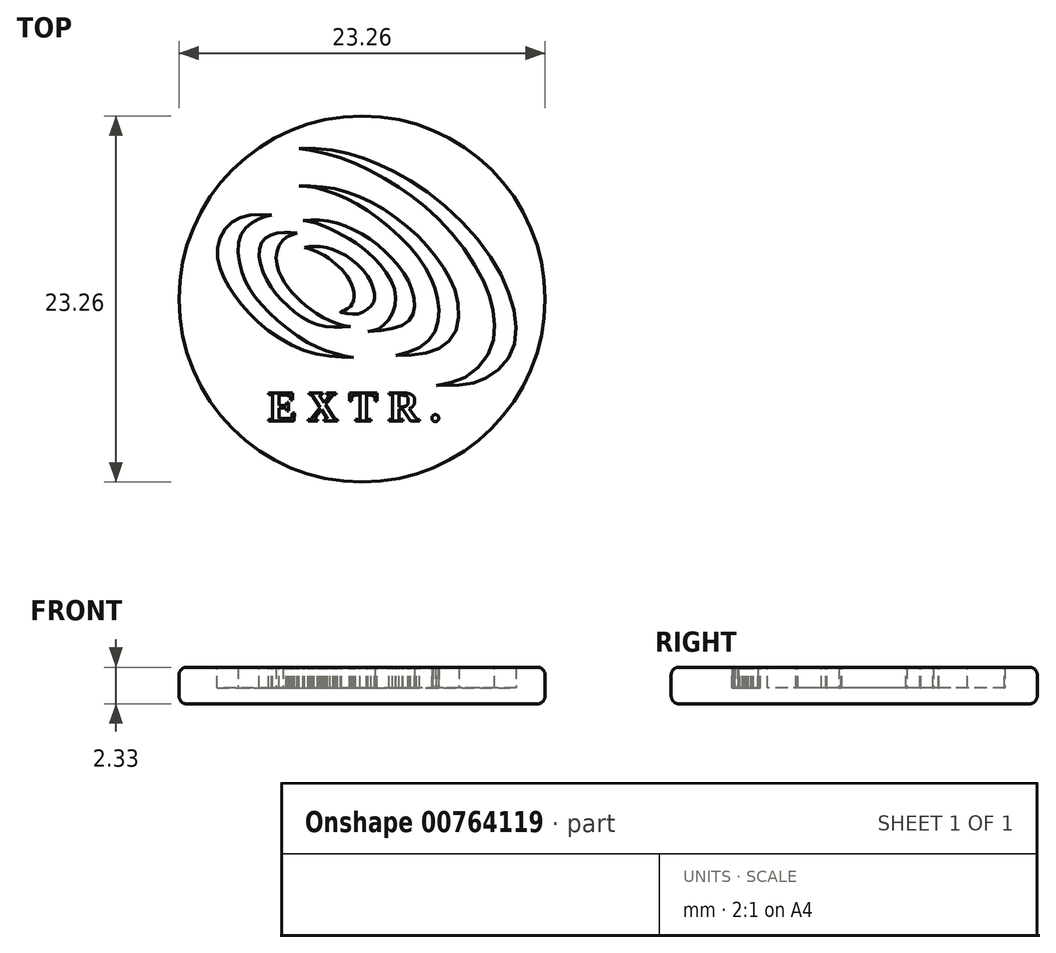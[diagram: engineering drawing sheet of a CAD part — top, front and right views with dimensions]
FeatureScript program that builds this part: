
annotation { "Feature Type Name" : "Feature", "Feature Type Description" : "" }
export const myFeature = defineFeature(function(context is Context, id is Id, definition is map)
    precondition{}
    {
        {
            assignVariable(context, id + "F0", {"name" : "Spessore", "anyValue" : 2.33});
        }
        {
            var Q0;
            Q0=qCreatedBy(makeId("Top.planeOp"),FACE);
            var sketch = newSketch(context, id + "F1", { "sketchPlane" : qUnion([Q0])});
            skCircle(sketch, "E0", {"center": v(0, 0) * mm, "radius": 11.62 * mm});
            skSolve(sketch);
        }
        {
            var Q0;
            Q0=makeQuery(id+"F1.imprint","IMPRINT",FACE,{"disambiguationData":[TD([[makeQuery(id+"F1.imprint","IMPRINT",EDGE,{"derivedFrom":sQuery(id+"F1.wireOp",EDGE,"E0")}),1.0]])]});
            extrude(context, id + "F2", {"entities" : qUnion([Q0]), "depth" : (getVariable(context, 'Spessore')) * mm, "offsetDistance" : 25 * mm});
        }
        {
            var Q0;
            Q0=makeQuery(id+"F2.opExtrude","CAP_EDGE",EDGE,{"disambiguationData":[OSD([sQuery(id+"F1.wireOp",EDGE,"E0")])],"isStart":true});
            var Q1;
            Q1=makeQuery(id+"F2.opExtrude","CAP_EDGE",EDGE,{"disambiguationData":[OSD([sQuery(id+"F1.wireOp",EDGE,"E0")])],"isStart":false});
            fillet(context, id + "F3", {"entities" : qUnion([Q0, Q1]), "radius" : .5 * mm, "tangentPropagation" : true, "allowEdgeOverflow" : false});
        }
        {
            var Q0;
            Q0=makeQuery(id+"F2.opExtrude","CAP_FACE",FACE,{"disambiguationData":[OSD([sQuery(id+"F1.wireOp",EDGE,"E0")])],"isStart":false});
            var sketch = newSketch(context, id + "F4", { "sketchPlane" : qUnion([Q0])});
            skFitSpline(sketch, "E1", {"points": [v(-4.15, 9.54) * mm, v(-1.9, 9.48) * mm, v(0.33, 8.86) * mm, v(2.32, 7.94) * mm, v(5.34, 5.86) * mm, v(8.2, 2.63) * mm, v(9.52, -0.22) * mm, v(9.72, -2.68) * mm, v(8.82, -4.33) * mm, v(7.32, -5.25) * mm, v(4.51, -5.5) * mm], "startDerivative": vector(24.3, 2.05) * mm, "endDerivative": vector(-46.96, -0.52) * mm});
            skFitSpline(sketch, "E2", {"points": [v(-4.17, 9.57) * mm, v(-2.58, 9.32) * mm, v(-0.42, 8.61) * mm, v(1.78, 7.45) * mm, v(3.82, 6.03) * mm, v(6.13, 3.65) * mm, v(7.85, 0.83) * mm, v(8.4, -1.19) * mm, v(8.13, -3.28) * mm, v(6.47, -5) * mm, v(4.52, -5.54) * mm], "startDerivative": vector(18.62, -2.24) * mm, "endDerivative": vector(-21.4, -4.3) * mm});
            skFitSpline(sketch, "E3", {"points": [v(-4.01, 7.2) * mm, v(-2.3, 7.1) * mm, v(-0.42, 6.62) * mm, v(1.63, 5.53) * mm, v(3.67, 3.88) * mm, v(5.06, 2.18) * mm, v(5.94, 0.42) * mm, v(6, -1.87) * mm, v(4.74, -3.21) * mm, v(2.17, -3.59) * mm], "startDerivative": vector(17.18, -0.33) * mm, "endDerivative": vector(-22.8, -0.77) * mm});
            skFitSpline(sketch, "E4", {"points": [v(-4.01, 7.2) * mm, v(-2.88, 7.06) * mm, v(-1.05, 6.4) * mm, v(1.04, 5.13) * mm, v(3.35, 2.94) * mm, v(4.53, 0.94) * mm, v(4.88, -0.87) * mm, v(4.23, -2.65) * mm, v(2.17, -3.59) * mm], "startDerivative": vector(11.55, -0.7) * mm, "endDerivative": vector(-17.99, -4.52) * mm});
            skFitSpline(sketch, "E5", {"points": [v(-3.73, 4.99) * mm, v(-2.39, 5) * mm, v(-0.8, 4.52) * mm, v(0.7, 3.68) * mm, v(2.18, 2.28) * mm, v(3.03, 0.97) * mm, v(3.33, -0.5) * mm, v(2.81, -1.53) * mm, v(0.37, -2.07) * mm], "startDerivative": vector(11.68, 1.03) * mm, "endDerivative": vector(-18.56, -1.71) * mm});
            skFitSpline(sketch, "E6", {"points": [v(-3.73, 4.99) * mm, v(-2.7, 4.75) * mm, v(-1.4, 4.16) * mm, v(-0.26, 3.46) * mm, v(0.97, 2.4) * mm, v(2.06, 0.62) * mm, v(1.9, -0.97) * mm, v(1.08, -1.86) * mm, v(0.37, -2.07) * mm], "startDerivative": vector(9.12, -1.58) * mm, "endDerivative": vector(-7.65, -1.26) * mm});
            skFitSpline(sketch, "E7", {"points": [v(-3.65, 3.29) * mm, v(-2.63, 3.33) * mm, v(-1.08, 2.78) * mm, v(0.35, 1.46) * mm, v(0.81, 0.15) * mm, v(0.59, -0.41) * mm, v(-0.18, -0.92) * mm, v(-1.31, -0.85) * mm], "startDerivative": vector(7.37, 1.02) * mm, "endDerivative": vector(-8.47, 1.72) * mm});
            skFitSpline(sketch, "E8", {"points": [v(-3.65, 3.29) * mm, v(-2.6, 2.89) * mm, v(-1.6, 2.16) * mm, v(-0.89, 1.36) * mm, v(-0.5, 0.22) * mm, v(-0.72, -0.45) * mm, v(-1.29, -0.79) * mm], "startDerivative": vector(5.9, -1.77) * mm, "endDerivative": vector(-4.6, -2.02) * mm});
            skFitSpline(sketch, "E9", {"points": [v(-1.29, -0.79) * mm, v(-1.31, -0.85) * mm], "startDerivative": vector(-0.1, -0.03) * mm, "endDerivative": vector(0.33, -0.05) * mm});
            skFitSpline(sketch, "E10", {"points": [v(-4.12, 4.18) * mm, v(-4.95, 3.82) * mm, v(-5.43, 2.87) * mm, v(-5.22, 1.61) * mm, v(-4.6, 0.6) * mm, v(-3.8, -0.21) * mm, v(-2.65, -1.07) * mm, v(-1.38, -1.62) * mm, v(-0.73, -1.74) * mm], "startDerivative": vector(-7.94, -2.2) * mm, "endDerivative": vector(6.18, -0.74) * mm});
            skFitSpline(sketch, "E11", {"points": [v(-4.12, 4.18) * mm, v(-5.32, 4.2) * mm, v(-6.28, 3.73) * mm, v(-6.51, 2.47) * mm, v(-5.75, 0.74) * mm, v(-4.42, -0.7) * mm, v(-2.62, -1.68) * mm, v(-0.73, -1.74) * mm], "startDerivative": vector(-9.7, 0.88) * mm, "endDerivative": vector(12.13, 0.46) * mm});
            skFitSpline(sketch, "E12", {"points": [v(-5.74, 5.35) * mm, v(-7.53, 5.26) * mm, v(-8.76, 4.35) * mm, v(-9.19, 2.78) * mm, v(-8.64, 1.11) * mm, v(-7.58, -0.42) * mm, v(-5.71, -2.17) * mm, v(-3, -3.46) * mm, v(-0.55, -3.7) * mm], "startDerivative": vector(-15.98, 0.97) * mm, "endDerivative": vector(17.67, -0.33) * mm});
            skFitSpline(sketch, "E13", {"points": [v(-5.74, 5.35) * mm, v(-6.53, 5.1) * mm, v(-7.38, 4.51) * mm, v(-7.86, 3.45) * mm, v(-7.63, 1.69) * mm, v(-6.97, 0.38) * mm, v(-5.74, -1.03) * mm, v(-3.67, -2.63) * mm, v(-1.94, -3.4) * mm, v(-0.55, -3.7) * mm], "startDerivative": vector(-9.77, -1.74) * mm, "endDerivative": vector(12.64, -2.27) * mm});
            skSolve(sketch);
        }
        {
            var Q0;
            Q0=makeQuery(id+"F4.imprint","IMPRINT",FACE,{"disambiguationData":[TD([[makeQuery(id+"F4.imprint","IMPRINT",EDGE,{"derivedFrom":sQuery(id+"F4.wireOp",EDGE,"E7")}),-1.0]])]});
            var Q1;
            Q1=makeQuery(id+"F4.imprint","IMPRINT",FACE,{"disambiguationData":[TD([[makeQuery(id+"F4.imprint","IMPRINT",EDGE,{"derivedFrom":sQuery(id+"F4.wireOp",EDGE,"E10")}),-1.0]])]});
            var Q2;
            Q2=makeQuery(id+"F4.imprint","IMPRINT",FACE,{"disambiguationData":[TD([[makeQuery(id+"F4.imprint","IMPRINT",EDGE,{"derivedFrom":sQuery(id+"F4.wireOp",EDGE,"E12")}),1.0]])]});
            var Q3;
            Q3=makeQuery(id+"F4.imprint","IMPRINT",FACE,{"disambiguationData":[TD([[makeQuery(id+"F4.imprint","IMPRINT",EDGE,{"derivedFrom":sQuery(id+"F4.wireOp",EDGE,"E5")}),-1.0]])]});
            var Q4;
            Q4=makeQuery(id+"F4.imprint","IMPRINT",FACE,{"disambiguationData":[TD([[makeQuery(id+"F4.imprint","IMPRINT",EDGE,{"derivedFrom":sQuery(id+"F4.wireOp",EDGE,"E3")}),-1.0]])]});
            var Q5;
            {var subQ0=sQuery(id+"F4.wireOp",EDGE,"E2");var subQ1=sQuery(id+"F4.wireOp",EDGE,"E1");var subQ2=makeQuery(id+"F4.imprint","INTERSECT",VERTEX,{"disambiguationData":[OD(0.0)],"derivedFrom":[subQ1,subQ0]});Q5=makeQuery(id+"F4.imprint","IMPRINT",FACE,{"disambiguationData":[TD([[makeQuery(id+"F4.imprint","IMPRINT",EDGE,{"disambiguationData":[TD([[subQ2,-1.0]])],"derivedFrom":subQ1}),-1.0]])]});}
            extrude(context, id + "F5", {"entities" : qUnion([Q0, Q1, Q2, Q3, Q4, Q5]), "operationType" : NewBodyOperationType.REMOVE, "oppositeDirection" : true, "depth" : 1.3 * mm, "offsetDistance" : 25 * mm});
        }
        {
            var Q0;
            Q0=makeQuery(id+"F2.opExtrude","CAP_FACE",FACE,{"disambiguationData":[OSD([sQuery(id+"F1.wireOp",EDGE,"E0")])],"isStart":false});
            var sketch = newSketch(context, id + "F6", { "sketchPlane" : qUnion([Q0])});
            skText(sketch, "E14", { "text": "E X T R .", "fontName": "Tinos-Bold.ttf"});
            const initialGuessF6  = {"E14": [-0.00597, -0.00774, 1, 0, 0.00196]};
            skSetInitialGuess(sketch, initialGuessF6);
            skSolve(sketch);
        }
        {
            var Q0;
            Q0 = qSketchRegion(id + "F6", true);
            extrude(context, id + "F7", {"entities" : qUnion([Q0]), "operationType" : NewBodyOperationType.REMOVE, "oppositeDirection" : true, "depth" : 1.3 * mm, "offsetDistance" : 25 * mm});
        }
    });
